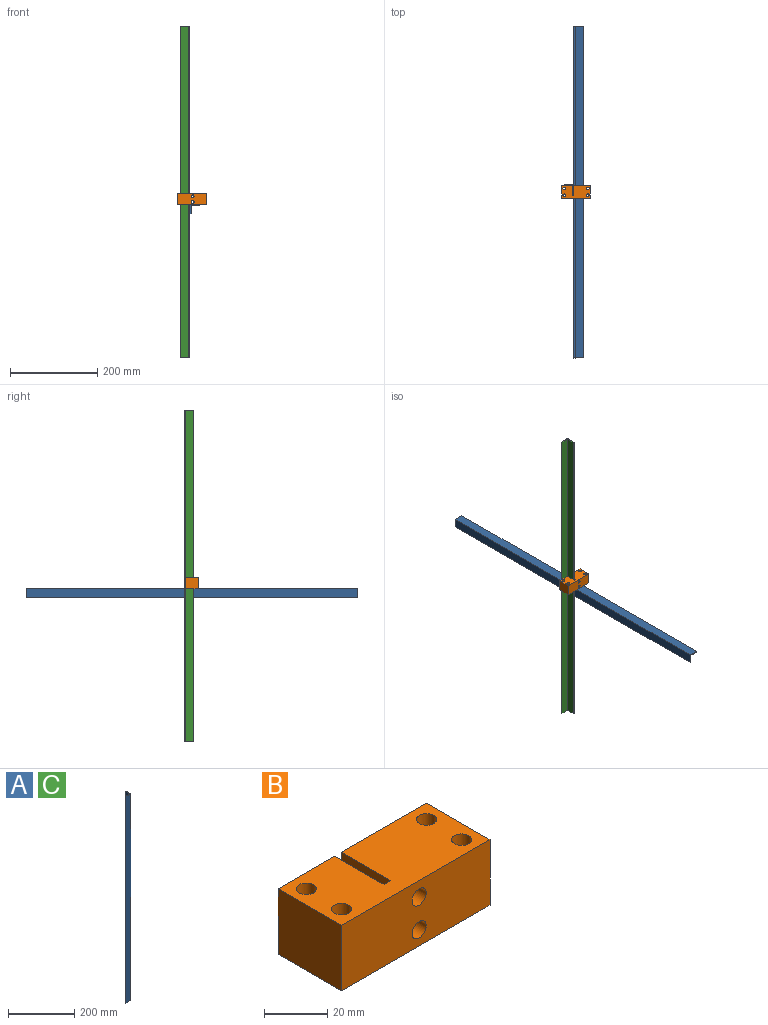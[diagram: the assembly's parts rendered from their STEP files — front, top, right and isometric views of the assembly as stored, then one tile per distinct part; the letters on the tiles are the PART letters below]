
ASSEMBLY  parts=3 mates=6
PART A: 8 faces, bbox 21.1x21.1x762 mm
  f0: plane 762x18.54mm, normal (-1,0,0), area 14129mm2, adj f1,f5,f6,f7
  f1: plane 762x18.54mm, normal (0,1,0), area 14129mm2, adj f0,f2,f6,f7
  f2: plane 762x2.54mm, normal (-1,0,0), area 1935.5mm2, adj f1,f3,f6,f7
  f3: plane 762x21.08mm, normal (0,-1,0), area 16064.5mm2, adj f2,f4,f6,f7
  f4: plane 762x21.08mm, normal (1,0,0), area 16064.5mm2, adj f3,f5,f6,f7
  f5: plane 762x2.54mm, normal (0,1,0), area 1935.5mm2, adj f0,f4,f6,f7
  f6: plane 21.08x21.08mm, normal (0,0,1), area 100.6mm2, adj f0,f1,f2,f3,f4,f5
  f7: plane 21.08x21.08mm, normal (0,0,-1), area 100.6mm2, adj f0,f1,f2,f3,f4,f5
PART B: 16 faces, bbox 66.5x28.4x25.4 mm
  f0: plane 28.45x25.4mm, normal (-1,0,0), area 722.6mm2, adj f1,f7,f8,f9
  f1: plane 66.55x25.4mm, normal (0,-1,0), area 1627mm2, adj f0,f2,f8,f9,f14,f15
  f2: plane 28.45x25.4mm, normal (1,0,0), area 722.6mm2, adj f1,f3,f8,f9
  f3: plane 38.1x25.4mm, normal (0,1,0), area 904.4mm2, adj f2,f4,f8,f9,f14,f15
  f4: plane 25.4x22.1mm, normal (-1,0,0), area 561.3mm2, adj f3,f5,f8,f9
  f5: plane 25.4x3.05mm, normal (0,1,0), area 77.4mm2, adj f4,f6,f8,f9
  f6: plane 25.4x22.1mm, normal (1,0,0), area 561.3mm2, adj f5,f7,f8,f9
  f7: plane 25.4x25.4mm, normal (0,1,0), area 645.2mm2, adj f0,f6,f8,f9
  f8: plane 66.55x28.45mm, normal (0,0,1), area 1699.1mm2, adj f0,f1,f2,f3,f4,f5,f6,f7
  f9: plane 66.55x28.45mm, normal (0,0,-1), area 1699.1mm2, adj f0,f1,f2,f3,f4,f5,f6,f7
  f10: cylinder r=3.17mm len=25.4mm, axis (0,0,1), area 506.7mm2, adj f8,f9
  f11: cylinder r=3.17mm len=25.4mm, axis (0,0,1), area 506.7mm2, adj f8,f9
  f12: cylinder r=3.17mm len=25.4mm, axis (0,0,1), area 506.7mm2, adj f8,f9
  f13: cylinder r=3.17mm len=25.4mm, axis (0,0,1), area 506.7mm2, adj f8,f9
  f14: cylinder r=3.17mm len=28.45mm, axis (0,1,0), area 567.5mm2, adj f1,f3
  f15: cylinder r=3.17mm len=28.45mm, axis (0,1,0), area 567.5mm2, adj f1,f3
PART C: same geometry as A
PLACE A rot(axis=(-0.58,-0.58,-0.58),120deg) t=(38.87,-372.09,-22.54)mm
PLACE B t=(10.42,-5.15,-1.46)mm
PLACE C rot(axis=(0,0,1),90deg) t=(38.87,4.75,-353.47)mm
MATE parallel A.f7 <-> C.f2  axis (0,-1,0) through (45.07,-372.09,-7.66)mm
MATE planar C.f3 <-> B.f4  axis (1,0,0) through (38.87,15.3,27.53)mm
MATE planar A.f3 <-> C.f3  axis (-1,0,0) through (38.87,8.91,-12)mm
MATE planar A.f4 <-> B.f9  axis (0,0,1) through (49.41,8.91,-1.46)mm
MATE parallel C.f0 <-> B.f7  axis (0,-1,0) through (27.06,23.3,27.53)mm
MATE planar C.f0 <-> B.f7  axis (0,-1,0) through (27.06,23.3,27.53)mm
